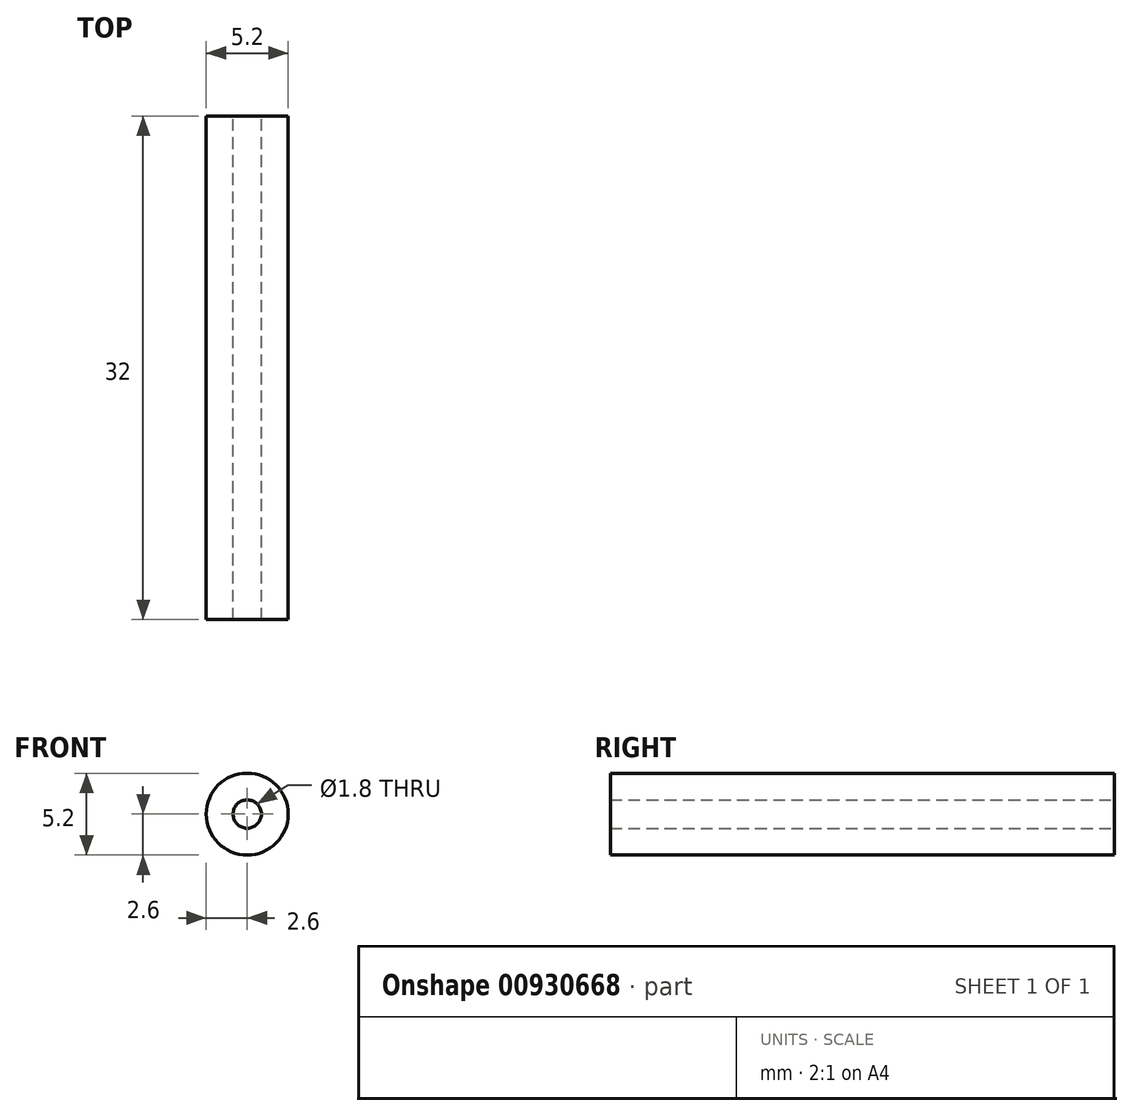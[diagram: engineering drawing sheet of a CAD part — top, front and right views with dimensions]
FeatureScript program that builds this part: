
annotation { "Feature Type Name" : "Feature", "Feature Type Description" : "" }
export const myFeature = defineFeature(function(context is Context, id is Id, definition is map)
    precondition{}
    {
        {
            var Q0;
            Q0=qCreatedBy(makeId("Front.planeOp"),FACE);
            var sketch = newSketch(context, id + "F0", { "sketchPlane" : qUnion([Q0])});
            skCircle(sketch, "E0", {"center": v(0, 0) * mm, "radius": 2.6 * mm});
            skCircle(sketch, "E1", {"center": v(0, 0) * mm, "radius": 0.9 * mm});
            skSolve(sketch);
        }
        {
            var Q0;
            Q0=qSketchRegion(id+"F0",true);
            extrude(context, id + "F1", {"entities" : qUnion([Q0]), "depth" : 32 * mm, "offsetDistance" : 25 * mm});
        }
    });
